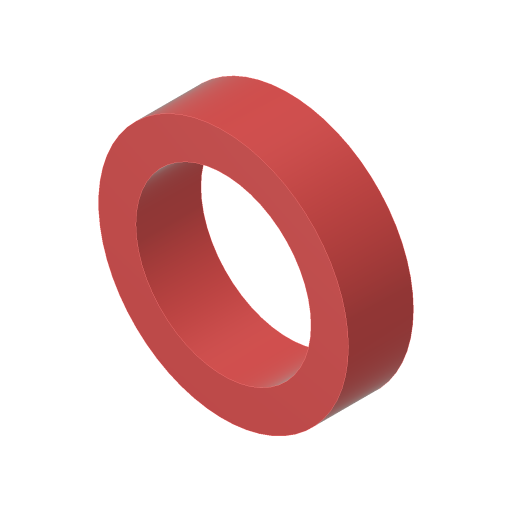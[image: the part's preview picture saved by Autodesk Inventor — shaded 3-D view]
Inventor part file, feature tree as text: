
AUTODESK INVENTOR PART (.ipt)
format: ipt  version: 2023.4 (Build 274418000, 418)  size: 113,664 bytes
history: native  units: in
note: dims shown in document units (in); Inventor stores cm internally (conversion verified against a paired STEP export)
features: extrude x1, sketch x1
ambient origin geometry x8: Origin, YZ Plane, XZ Plane, XY Plane, X Axis, Y Axis, Z Axis, Center Point
bodies: Solid1 (feature_tree)
feature tree (2):
  extrude  "Extrusion1"  Depth=0.2175in
  sketch  "Sketch1"  dims[d0=0.585in d1=0.125in d2=0.2175in d3=0.0in]
